# Revit family: Providence Medium
name_source: partatom
category: Lighting Fixtures
units: mm (PartAtom-declared; Revit-internal decimal feet)

## family parameters
Cut with Voids When Loaded = No
Host = Face
Light Source = No
OmniClass Number = 23.80.70.14
OmniClass Title = Luminaries for External Lighting
Part Type = Normal
Room Calculation Point = No
Round Connector Dimension = Use Diameter
Shared = No

## types (13) — shared parameters
Apparent Load = 0 VA
Default Elevation = 48.000"
Description = PROVIDENCE MEDIUM
Lamp = 32 LED
Light Bulb Material = Glass-Frosted
Load Classification = Lighting
Manufacturer = Architectural Area Lighting
Model = PROV
Pole Height = 48.000"
URL = https://www.currentlighting.com
Wattage Comments = 26-75W

## per-type parameters (varying)
| type | Finish |
| Arctic White | Aluminum-Artic White |
| Black | Aluminum-Black |
| Matte Black | Aluminum-Matte Black |
| Dark Green | Glass-Frosted |
| Dark Bronze | Aluminum-Dark Bronze |
| Wheathered Bronze | Aluminum-Weathered Bronze |
| Metallic Bronze | Aluminum-Metalic Bronze |
| Verde Blue | Aluminum-Verde Blue |
| Corten | Aluminum-Corten |
| Matte Aluminum | Aluminum-Matte |
| Medium Grey | Aluminum-Medium Grey |
| Antique Green | Aluminum-Antique Green |
| Light Grey | Aluminum-Light Grey |

## geometry (parser evidence)
native form markers: Blend x36, Sweep x9
no freeform markers — native parametric forms only
